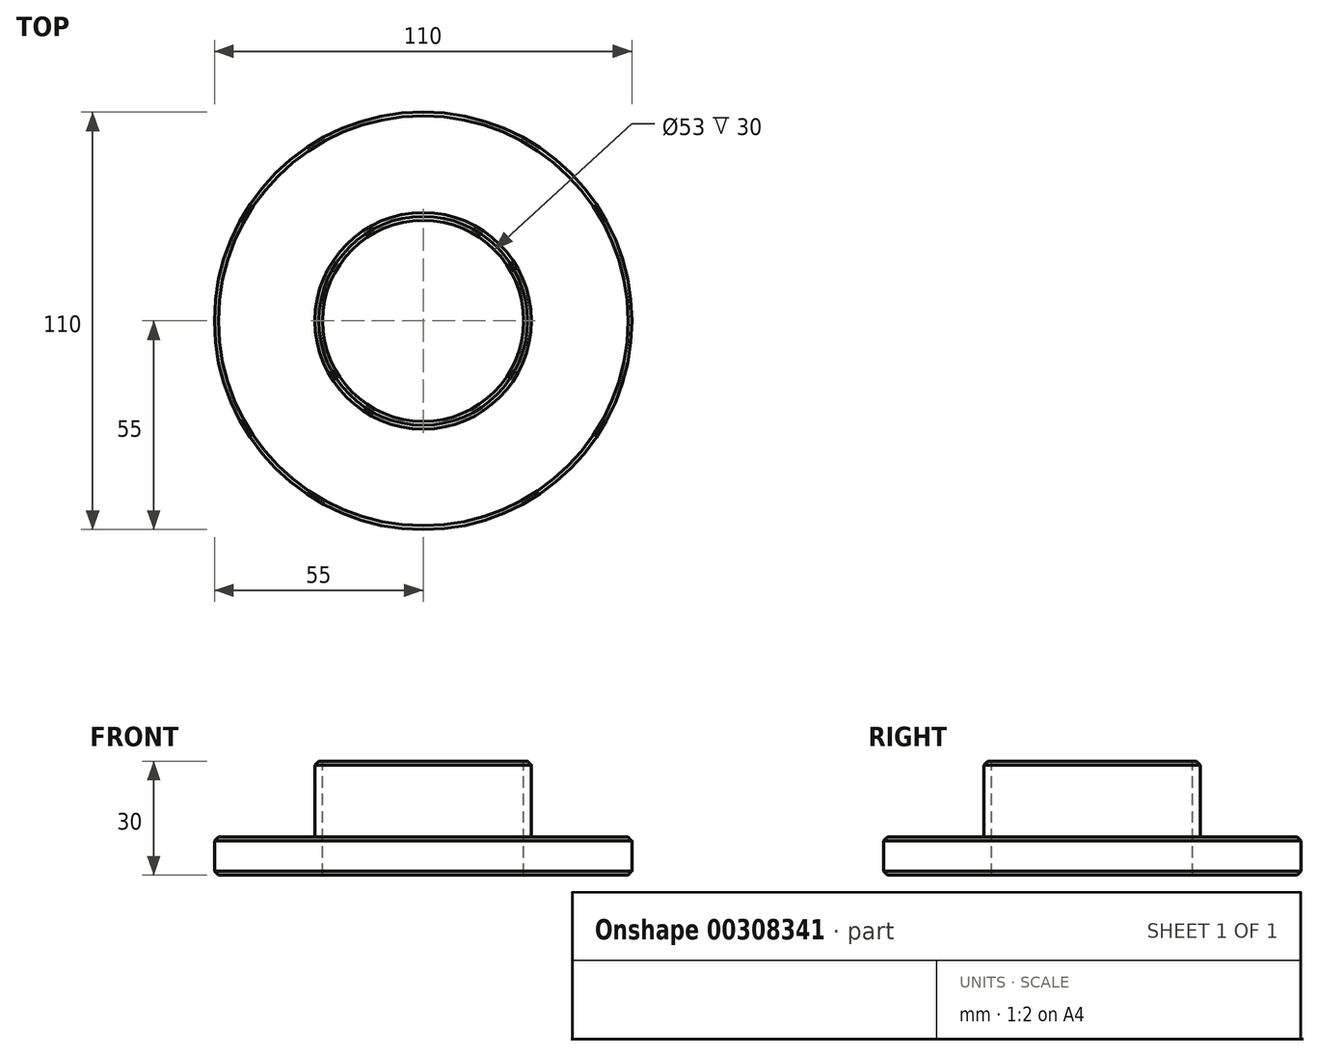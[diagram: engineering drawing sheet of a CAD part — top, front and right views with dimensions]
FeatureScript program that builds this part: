
annotation { "Feature Type Name" : "Feature", "Feature Type Description" : "" }
export const myFeature = defineFeature(function(context is Context, id is Id, definition is map)
    precondition{}
    {
        {
            var Q0;
            Q0=qCreatedBy(makeId("Front.planeOp"),FACE);
            var sketch = newSketch(context, id + "F0", { "sketchPlane" : qUnion([Q0])});
            skLineSegment(sketch, "E0", {"start": v(0, 120.04) * mm, "end": v(0, 0) * mm});
            skLineSegment(sketch, "E1.0", {"start": v(-55, 10) * mm, "end": v(-55, 0) * mm});
            skLineSegment(sketch, "E2.0", {"start": v(-28.5, 30) * mm, "end": v(-28.5, 10) * mm});
            skLineSegment(sketch, "E3.0", {"start": v(-26.5, 30) * mm, "end": v(-26.5, 0) * mm});
            skLineSegment(sketch, "E4", {"start": v(0, 0) * mm, "end": v(-55, 0) * mm});
            skLineSegment(sketch, "E5.0", {"start": v(-28.5, 10) * mm, "end": v(-55, 10) * mm});
            skLineSegment(sketch, "E6.0", {"start": v(-26.5, 30) * mm, "end": v(-28.5, 30) * mm});
            skSolve(sketch);
        }
        {
            var Q0;
            {var subQ1=sQuery(id+"F0.wireOp",EDGE,"E1.0");Q0=makeQuery(id+"F0.imprint","IMPRINT",FACE,{"disambiguationData":[TD([[makeQuery(id+"F0.imprint","IMPRINT",EDGE,{"derivedFrom":subQ1}),1.0]])]});}
            var Q1;
            Q1=sQuery(id+"F0.wireOp",EDGE,"E0");
            revolve(context, id + "F1", {"entities" : qUnion([Q0]), "axis" : qUnion([Q1]), "revolveType" : RevolveType.FULL});
        }
        {
            var Q0;
            Q0=makeQuery(id+"F1.opRevolve","SWEPT_EDGE",EDGE,{"disambiguationData":[OSD([sQuery(id+"F0.wireOp",EDGE,"E1.0"),sQuery(id+"F0.wireOp",EDGE,"E5.0")])]});
            chamfer(context, id + "F2", {"entities" : qUnion([Q0]), "width" : 1 * mm, "tangentPropagation" : true});
        }
        {
            var Q0;
            Q0=makeQuery(id+"F1.opRevolve","SWEPT_EDGE",EDGE,{"disambiguationData":[OSD([sQuery(id+"F0.wireOp",EDGE,"E2.0"),sQuery(id+"F0.wireOp",EDGE,"E6.0")])]});
            var Q1;
            Q1=makeQuery(id+"F1.opRevolve","SWEPT_EDGE",EDGE,{"disambiguationData":[OSD([sQuery(id+"F0.wireOp",EDGE,"E1.0"),sQuery(id+"F0.wireOp",EDGE,"E4")])]});
            chamfer(context, id + "F3", {"entities" : qUnion([Q0, Q1]), "width" : 1 * mm, "tangentPropagation" : true});
        }
    });
